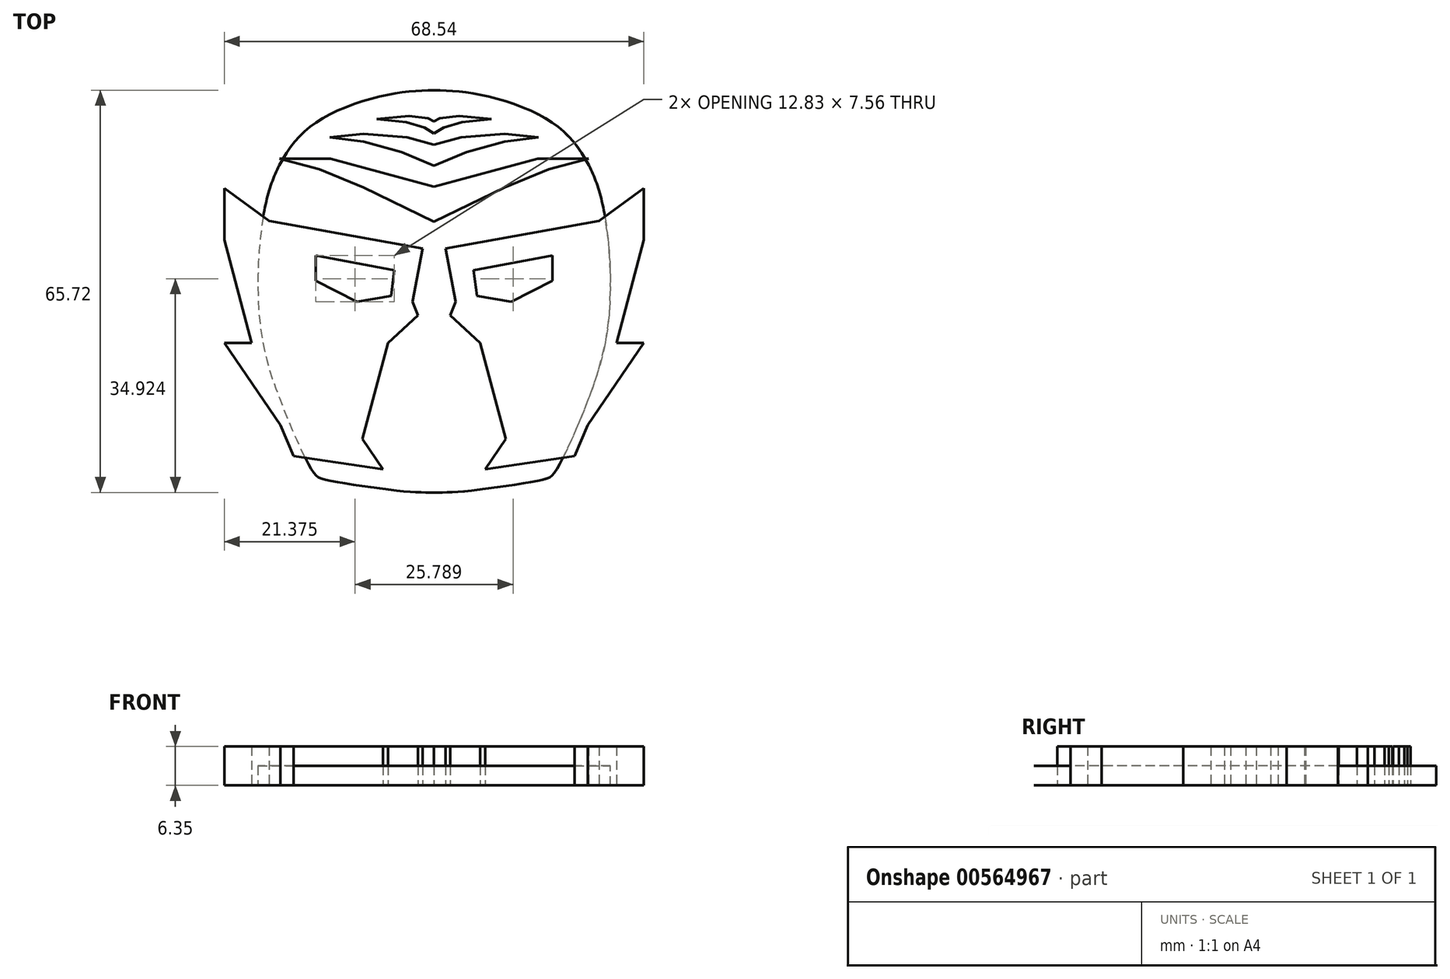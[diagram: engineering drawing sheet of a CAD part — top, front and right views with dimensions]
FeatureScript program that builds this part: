
annotation { "Feature Type Name" : "Feature", "Feature Type Description" : "" }
export const myFeature = defineFeature(function(context is Context, id is Id, definition is map)
    precondition{}
    {
        {
            var Q0;
            Q0=qCreatedBy(makeId("Top.planeOp"),FACE);
            var sketch = newSketch(context, id + "F0", { "sketchPlane" : qUnion([Q0])});
            skLineSegment(sketch, "E0", {"start": v(-1.9, 6.69) * mm, "end": v(-3.52, -2.03) * mm});
            skLineSegment(sketch, "E1", {"start": v(-3.52, -2.03) * mm, "end": v(-2.64, -4.24) * mm});
            skLineSegment(sketch, "E2", {"start": v(-2.64, -4.24) * mm, "end": v(-7.51, -8.75) * mm});
            skLineSegment(sketch, "E3", {"start": v(-7.51, -8.75) * mm, "end": v(-11.72, -24.41) * mm});
            skLineSegment(sketch, "E4", {"start": v(-11.72, -24.41) * mm, "end": v(-8.32, -29.36) * mm});
            skLineSegment(sketch, "E5", {"start": v(-8.32, -29.36) * mm, "end": v(-22.95, -27.22) * mm});
            skLineSegment(sketch, "E6", {"start": v(-22.95, -27.22) * mm, "end": v(-25.1, -22.12) * mm});
            skLineSegment(sketch, "E7", {"start": v(-25.1, -22.12) * mm, "end": v(-34.27, -8.75) * mm});
            skLineSegment(sketch, "E8", {"start": v(-34.27, -8.75) * mm, "end": v(-29.82, -8.75) * mm});
            skLineSegment(sketch, "E9", {"start": v(-29.82, -8.75) * mm, "end": v(-34.27, 8.1) * mm});
            skLineSegment(sketch, "E10", {"start": v(-34.27, 8.1) * mm, "end": v(-34.27, 16.51) * mm});
            skLineSegment(sketch, "E11", {"start": v(-34.27, 16.51) * mm, "end": v(-26.94, 11.2) * mm});
            skLineSegment(sketch, "E12", {"start": v(-26.94, 11.2) * mm, "end": v(-1.9, 6.69) * mm});
            skLineSegment(sketch, "E13", {"start": v(-6.48, 3.14) * mm, "end": v(-19.31, 5.54) * mm});
            skLineSegment(sketch, "E14", {"start": v(-19.31, 5.54) * mm, "end": v(-19.31, 1.44) * mm});
            skLineSegment(sketch, "E15", {"start": v(-19.31, 1.44) * mm, "end": v(-12.6, -2.03) * mm});
            skLineSegment(sketch, "E16", {"start": v(-12.6, -2.03) * mm, "end": v(-7, -1.07) * mm});
            skLineSegment(sketch, "E17", {"start": v(-7, -1.07) * mm, "end": v(-6.48, 3.14) * mm});
            skLineSegment(sketch, "E18.MirrorCS", {"start": v(26.94, 11.2) * mm, "end": v(1.9, 6.69) * mm});
            skLineSegment(sketch, "E19.MirrorCS", {"start": v(3.52, -2.03) * mm, "end": v(2.64, -4.24) * mm});
            skLineSegment(sketch, "E20.MirrorCS", {"start": v(12.6, -2.03) * mm, "end": v(7, -1.07) * mm});
            skLineSegment(sketch, "E21.MirrorCS", {"start": v(22.95, -27.22) * mm, "end": v(25.1, -22.12) * mm});
            skLineSegment(sketch, "E22.MirrorCS", {"start": v(8.32, -29.36) * mm, "end": v(22.95, -27.22) * mm});
            skLineSegment(sketch, "E23.MirrorCS", {"start": v(34.27, 16.51) * mm, "end": v(26.94, 11.2) * mm});
            skLineSegment(sketch, "E24.MirrorCS", {"start": v(25.1, -22.12) * mm, "end": v(34.27, -8.75) * mm});
            skLineSegment(sketch, "E25.MirrorCS", {"start": v(34.27, -8.75) * mm, "end": v(29.82, -8.75) * mm});
            skLineSegment(sketch, "E26.MirrorCS", {"start": v(11.72, -24.41) * mm, "end": v(8.32, -29.36) * mm});
            skLineSegment(sketch, "E27.MirrorCS", {"start": v(7.51, -8.75) * mm, "end": v(11.72, -24.41) * mm});
            skLineSegment(sketch, "E28.MirrorCS", {"start": v(7, -1.07) * mm, "end": v(6.48, 3.14) * mm});
            skLineSegment(sketch, "E29.MirrorCS", {"start": v(6.48, 3.14) * mm, "end": v(19.31, 5.54) * mm});
            skLineSegment(sketch, "E30.MirrorCS", {"start": v(29.82, -8.75) * mm, "end": v(34.27, 8.1) * mm});
            skLineSegment(sketch, "E31.MirrorCS", {"start": v(19.31, 5.54) * mm, "end": v(19.31, 1.44) * mm});
            skLineSegment(sketch, "E32.MirrorCS", {"start": v(1.9, 6.69) * mm, "end": v(3.52, -2.03) * mm});
            skLineSegment(sketch, "E33.MirrorCS", {"start": v(2.64, -4.24) * mm, "end": v(7.51, -8.75) * mm});
            skLineSegment(sketch, "E34.MirrorCS", {"start": v(34.27, 8.1) * mm, "end": v(34.27, 16.51) * mm});
            skLineSegment(sketch, "E35.MirrorCS", {"start": v(19.31, 1.44) * mm, "end": v(12.6, -2.03) * mm});
            skLineSegment(sketch, "E36", {"start": v(0, 11.06) * mm, "end": v(-11.55, 16.65) * mm});
            skLineSegment(sketch, "E37", {"start": v(-11.55, 16.65) * mm, "end": v(-18.76, 19.63) * mm});
            skLineSegment(sketch, "E38", {"start": v(-18.76, 19.63) * mm, "end": v(-25.22, 21.37) * mm});
            skLineSegment(sketch, "E39", {"start": v(-25.22, 21.37) * mm, "end": v(-16.9, 21.37) * mm});
            skLineSegment(sketch, "E40", {"start": v(-16.9, 21.37) * mm, "end": v(-4.92, 18.14) * mm});
            skLineSegment(sketch, "E41", {"start": v(-4.92, 18.14) * mm, "end": v(0, 16.82) * mm});
            skLineSegment(sketch, "E42", {"start": v(0, 20.25) * mm, "end": v(-5.33, 22.46) * mm});
            skLineSegment(sketch, "E43", {"start": v(-5.33, 22.46) * mm, "end": v(-11.55, 24.13) * mm});
            skLineSegment(sketch, "E44", {"start": v(-11.55, 24.13) * mm, "end": v(-17.04, 24.83) * mm});
            skLineSegment(sketch, "E45", {"start": v(-17.04, 24.83) * mm, "end": v(-11.55, 25.4) * mm});
            skLineSegment(sketch, "E46", {"start": v(-11.55, 25.4) * mm, "end": v(-4.4, 24.83) * mm});
            skLineSegment(sketch, "E47", {"start": v(-4.4, 24.83) * mm, "end": v(0, 23.64) * mm});
            skLineSegment(sketch, "E48", {"start": v(0, 25.5) * mm, "end": v(-1.53, 26.45) * mm});
            skLineSegment(sketch, "E49", {"start": v(-1.53, 26.45) * mm, "end": v(-4.56, 27.34) * mm});
            skLineSegment(sketch, "E50", {"start": v(-4.56, 27.34) * mm, "end": v(-9.36, 27.86) * mm});
            skLineSegment(sketch, "E51", {"start": v(-9.36, 27.86) * mm, "end": v(-4.09, 28.38) * mm});
            skLineSegment(sketch, "E52", {"start": v(-4.09, 28.38) * mm, "end": v(-0.95, 27.96) * mm});
            skLineSegment(sketch, "E53", {"start": v(-0.95, 27.96) * mm, "end": v(0, 27.5) * mm});
            skLineSegment(sketch, "E54.MirrorCS", {"start": v(0.95, 27.96) * mm, "end": v(0, 27.5) * mm});
            skLineSegment(sketch, "E55.MirrorCS", {"start": v(0, 25.5) * mm, "end": v(1.53, 26.45) * mm});
            skLineSegment(sketch, "E56.MirrorCS", {"start": v(16.9, 21.37) * mm, "end": v(4.92, 18.14) * mm});
            skLineSegment(sketch, "E57.MirrorCS", {"start": v(0, 11.06) * mm, "end": v(11.55, 16.65) * mm});
            skLineSegment(sketch, "E58.MirrorCS", {"start": v(17.04, 24.83) * mm, "end": v(11.55, 25.4) * mm});
            skLineSegment(sketch, "E59.MirrorCS", {"start": v(4.09, 28.38) * mm, "end": v(0.95, 27.96) * mm});
            skLineSegment(sketch, "E60.MirrorCS", {"start": v(1.53, 26.45) * mm, "end": v(4.56, 27.34) * mm});
            skLineSegment(sketch, "E61.MirrorCS", {"start": v(25.22, 21.37) * mm, "end": v(16.9, 21.37) * mm});
            skLineSegment(sketch, "E62.MirrorCS", {"start": v(4.4, 24.83) * mm, "end": v(0, 23.64) * mm});
            skLineSegment(sketch, "E63.MirrorCS", {"start": v(9.36, 27.86) * mm, "end": v(4.09, 28.38) * mm});
            skLineSegment(sketch, "E64.MirrorCS", {"start": v(11.55, 24.13) * mm, "end": v(17.04, 24.83) * mm});
            skLineSegment(sketch, "E65.MirrorCS", {"start": v(18.76, 19.63) * mm, "end": v(25.22, 21.37) * mm});
            skLineSegment(sketch, "E66.MirrorCS", {"start": v(0, 20.25) * mm, "end": v(5.33, 22.46) * mm});
            skLineSegment(sketch, "E67.MirrorCS", {"start": v(11.55, 25.4) * mm, "end": v(4.4, 24.83) * mm});
            skLineSegment(sketch, "E68.MirrorCS", {"start": v(4.92, 18.14) * mm, "end": v(0, 16.82) * mm});
            skLineSegment(sketch, "E69.MirrorCS", {"start": v(4.56, 27.34) * mm, "end": v(9.36, 27.86) * mm});
            skLineSegment(sketch, "E70.MirrorCS", {"start": v(11.55, 16.65) * mm, "end": v(18.76, 19.63) * mm});
            skLineSegment(sketch, "E71.MirrorCS", {"start": v(5.33, 22.46) * mm, "end": v(11.55, 24.13) * mm});
            skSolve(sketch);
        }
        {
            var Q0;
            Q0 = qSketchRegion(id + "F0", true);
            extrude(context, id + "F1", {"entities" : qUnion([Q0]), "depth" : 6.35 * mm, "offsetDistance" : 25.4 * mm});
        }
        {
            var Q0;
            Q0=qCreatedBy(makeId("Top.planeOp"),FACE);
            var sketch = newSketch(context, id + "F2", { "sketchPlane" : qUnion([Q0])});
            skFitSpline(sketch, "E72", {"points": [v(0, 32.55) * mm, v(-6.96, 31.93) * mm, v(-18.01, 28.08) * mm, v(-23.98, 22.49) * mm, v(-27.58, 13.67) * mm, v(-28.58, -4.35) * mm, v(-25.22, -17.9) * mm, v(-19.75, -29.82) * mm, v(-17.77, -31.06) * mm, v(-5.34, -32.92) * mm, v(0, -33.17) * mm], "startDerivative": vector(-75.19, -2.21) * mm, "endDerivative": vector(57.87, -0.17) * mm});
            skFitSpline(sketch, "E73.MirrorCS", {"points": [v(0, 32.55) * mm, v(6.96, 31.93) * mm, v(18.01, 28.08) * mm, v(23.98, 22.49) * mm, v(27.58, 13.67) * mm, v(28.58, -4.35) * mm, v(25.22, -17.9) * mm, v(19.75, -29.82) * mm, v(17.77, -31.06) * mm, v(5.34, -32.92) * mm, v(0, -33.17) * mm], "startDerivative": vector(75.19, -2.21) * mm, "endDerivative": vector(-57.87, -0.17) * mm});
            skSolve(sketch);
        }
        {
            var Q0;
            Q0=makeQuery(id+"F2.imprint","IMPRINT",FACE,{"disambiguationData":[TD([[makeQuery(id+"F2.imprint","IMPRINT",EDGE,{"derivedFrom":sQuery(id+"F2.wireOp",EDGE,"E72")}),1.0]])]});
            extrude(context, id + "F3", {"entities" : qUnion([Q0]), "depth" : 3.17 * mm, "offsetDistance" : 25.4 * mm});
        }
    });
